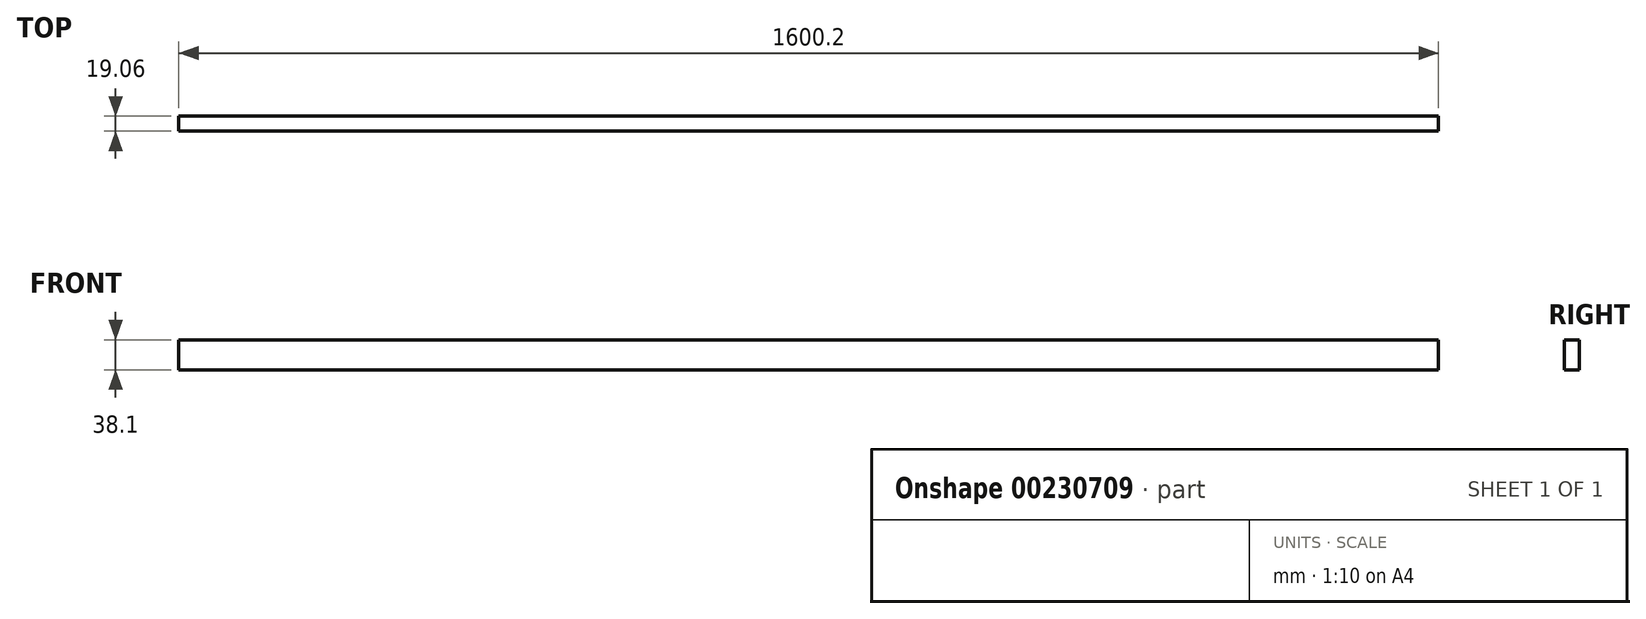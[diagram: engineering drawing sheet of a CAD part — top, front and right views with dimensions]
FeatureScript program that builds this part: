
annotation { "Feature Type Name" : "Feature", "Feature Type Description" : "" }
export const myFeature = defineFeature(function(context is Context, id is Id, definition is map)
    precondition{}
    {
        {
            var Q0;
            Q0=qCreatedBy(makeId("Right.planeOp"),FACE);
            var sketch = newSketch(context, id + "F0", { "sketchPlane" : qUnion([Q0])});
            skLineSegment(sketch, "E0.bottom", {"start": v(-9.52, 19.05) * mm, "end": v(9.53, 19.05) * mm});
            skLineSegment(sketch, "E0.top", {"start": v(-9.52, -19.05) * mm, "end": v(9.53, -19.05) * mm});
            skLineSegment(sketch, "E0.left", {"start": v(-9.52, 19.05) * mm, "end": v(-9.52, -19.05) * mm});
            skLineSegment(sketch, "E0.right", {"start": v(9.53, 19.05) * mm, "end": v(9.53, -19.05) * mm});
            skSolve(sketch);
        }
        {
            var Q0;
            Q0=makeQuery(id+"F0.imprint","IMPRINT",FACE,{"disambiguationData":[TD([[makeQuery(id+"F0.imprint","IMPRINT",EDGE,{"derivedFrom":sQuery(id+"F0.wireOp",EDGE,"E0.bottom")}),-1.0]])]});
            extrude(context, id + "F1", {"entities" : qUnion([Q0]), "depth" : 1600.2 * mm});
        }
    });
